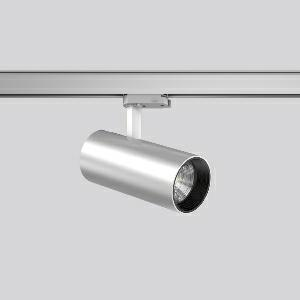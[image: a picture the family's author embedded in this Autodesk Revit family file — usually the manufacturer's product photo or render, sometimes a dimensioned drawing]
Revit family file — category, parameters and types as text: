
# Revit family: deecos_s_mini_742199_004_2_76_54ae
name_source: partatom
category: Lighting Fixtures
units: mm (PartAtom-declared; Revit-internal decimal feet)

## family parameters
Cut with Voids When Loaded = No
Host = Face
Light Source = No
Part Type = Normal
Room Calculation Point = No
Round Connector Dimension = Use Diameter
Shared = No

## types (1)
- DEECOS S mini (1 x LED Modul 927, 2000 lm, 2700)
    Apparent Load = 20 VA
    Approval mark = CE
    CIE Flux Codes = 96 100 100 100 100
    Color Rendering = 92
    Color Temperature = 2700
    Default Elevation = 1800 mm
    Description = Series: DEECOS S mini
LED surface-mounted projector in modern design with no visible cooling ribs. Housing: die-cast aluminium, powder-coated. Rotation range: 356°. Swivel range: 90°. Black plastic ring and recessed LED to prevent glare from the side. Optical assembly with lens made of plastic (polycarbonate) for the best homogeneous light distribution - can be changed without tools. Best colour rendering index Ra>90. With adapter for RZB 3-circuit DALI tracks. Suitable for Track on ceiling, Wall track. High quality converter without flickering and stroboscopic effect. The following accessories can be mounted without use of tools: interchangeable lenses, decorative glasses, honeycomb louvre, clear and frosted diffusers, white interchangeable plastic ring. 
Colour: silver
Diameter: 87 mm
Height: 214 mm
Lamp: LED
Socket: without socket
Colour temperature: 2700K
Colour rendering index (CRI): 92
System power: 20 W
Rated luminous flux: 2000 lm
Luminous efficiency: 100 lm/W
Control gear: Converter, dimmable, DALI
Protection class: I
Type of protection: IP 20
    Height = 214 mm
    Lamp = 1 x LED Modul 927
    Lamp Light Flux = 2000 lm
    Lamp count = 1
    Length = 87 mm
    Lifetime = 50000 h
    Luminous efficacy = 100 lm/W
    Manufacturer = RZB
    ModVariant = No
    Model = 742199.004.2.76
    Mounting Place = Ceiling
    Mounting Type = Rail mounted
    Number of Poles = 1
    OnlyDefault = Yes
    Power Factor = 1
    Product Name = DEECOS S mini
    Product group = Track mounted projectors
    ProductGroupID = 301
    Protection Class = Protection class I
    Protection Degree = IP 20
    RLX_Detail_Level = 1
    RLX_Emergency_Light_Flux = 0 lm
    RLX_Emergency_Type = 0
    RLX_Emergency_Type_DB = No
    RlxData = <blob elided: 37713 chars, md5=ec76d65b>
    Socket = socket
    Standby Power = 0 W
    System Light Flux = 2000 lm
    System Power = 20 W
    Type Comments = Product without accessories
    Type Image = 741930.004.jpg
    URL = http://relux.com
    VarID = ---
    Voltage = 230 V
    Voltage Range = 220-240 V
    Weight = 0.00 kg
    Width = 0 mm  [stored 0 ft]

note: [stored X ft] marks values corroborated as IEEE doubles in the binary element streams (Revit-internal decimal feet)

## geometry (parser evidence)
native form markers: Blend x4, Sweep x11
no freeform markers — native parametric forms only
